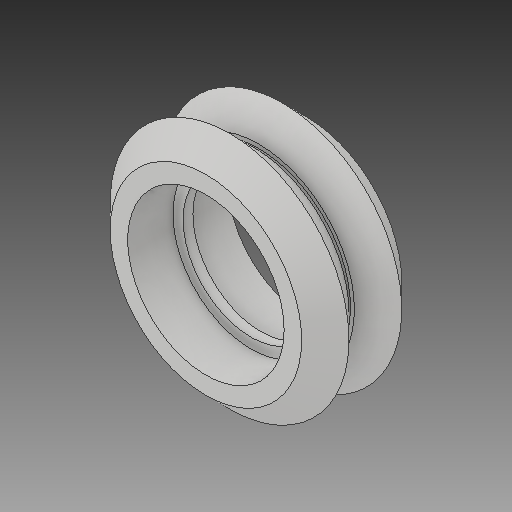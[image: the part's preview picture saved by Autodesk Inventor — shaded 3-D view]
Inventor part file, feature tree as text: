
AUTODESK INVENTOR PART (.ipt)
format: ipt  version: 2018 (Build 220112000, 112)  size: 177,152 bytes
history: native  units: mm
features: sketch x5, extrude x4, revolve x1
ambient origin geometry x8: Origin, YZ Plane, XZ Plane, XY Plane, X Axis, Y Axis, Z Axis, Center Point
bodies: Solid1 (feature_tree)
feature tree (10):
  extrude  "Extrusion1"  Depth=10.23mm TaperAngle=0.0deg
  revolve  "Revolution1"  [1 undecoded]
  extrude  "Extrusion2"  TaperAngle=90.0deg  [1 undecoded]
  extrude  "Extrusion3"  Depth=30.0mm TaperAngle=0.0deg
  extrude  "Extrusion4"  Depth=4.615mm TaperAngle=0.0deg
  sketch  "Sketch1"  dims[d0=24.39mm d1=10.23mm d2=0.0mm]
  sketch  "Sketch2"  dims[d4=0.275mm d5=0.55mm]
  sketch  "Sketch3"  dims[d6=135.0deg d7=90.0deg]
  sketch  "Sketch4"  dims[d8=13.89mm d9=30.0mm d10=0.0mm]
  sketch  "Sketch5"  dims[d11=15.974mm d12=4.615mm d13=0.0mm d14=15.974mm d15=4.615mm d16=0.0mm]
note: 2 required parameter values undecoded (feature->parameter linkage not recoverable at this tier; creation-order binding heuristic only, values carry confidence <= 0.55)